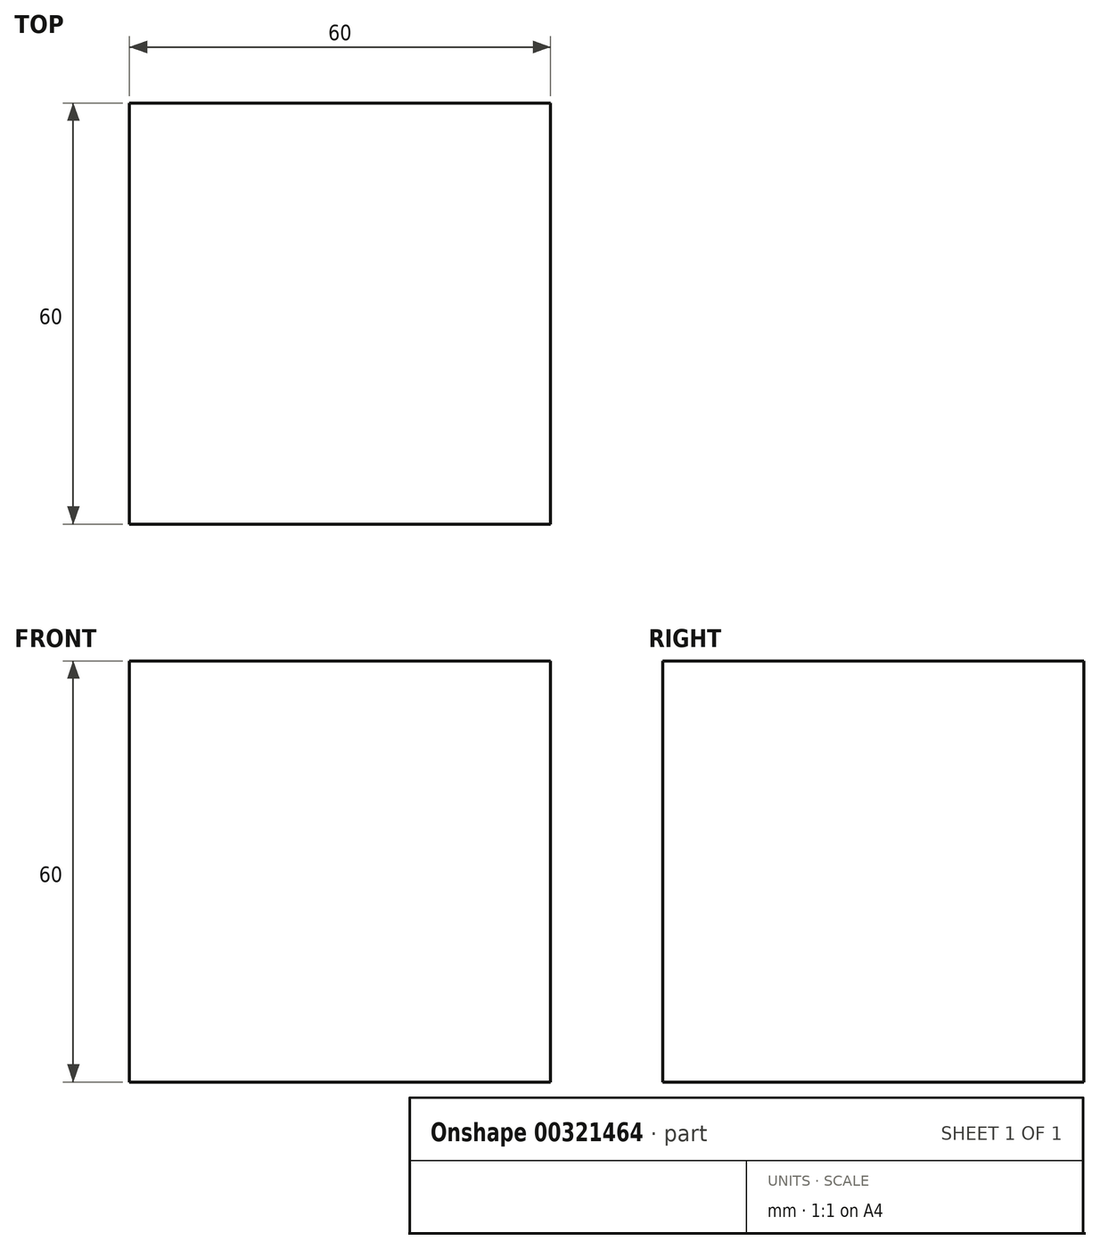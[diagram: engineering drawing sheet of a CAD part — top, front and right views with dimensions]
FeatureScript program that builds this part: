
annotation { "Feature Type Name" : "Feature", "Feature Type Description" : "" }
export const myFeature = defineFeature(function(context is Context, id is Id, definition is map)
    precondition{}
    {
        {
            var Q0;
            Q0=qCreatedBy(makeId("Top.planeOp"),FACE);
            var sketch = newSketch(context, id + "F0", { "sketchPlane" : qUnion([Q0])});
            skLineSegment(sketch, "E0.bottom", {"start": v(30, 30) * mm, "end": v(-30, 30) * mm});
            skLineSegment(sketch, "E0.top", {"start": v(30, -30) * mm, "end": v(-30, -30) * mm});
            skLineSegment(sketch, "E0.left", {"start": v(30, 30) * mm, "end": v(30, -30) * mm});
            skLineSegment(sketch, "E0.right", {"start": v(-30, 30) * mm, "end": v(-30, -30) * mm});
            skPoint(sketch, "E0.middle", {"position": v(0, 0) * mm});
            skSolve(sketch);
        }
        {
            var Q0;
            Q0 = qSketchRegion(id + "F0", true);
            extrude(context, id + "F1", {"entities" : qUnion([Q0]), "depth" : 60 * mm});
        }
    });
